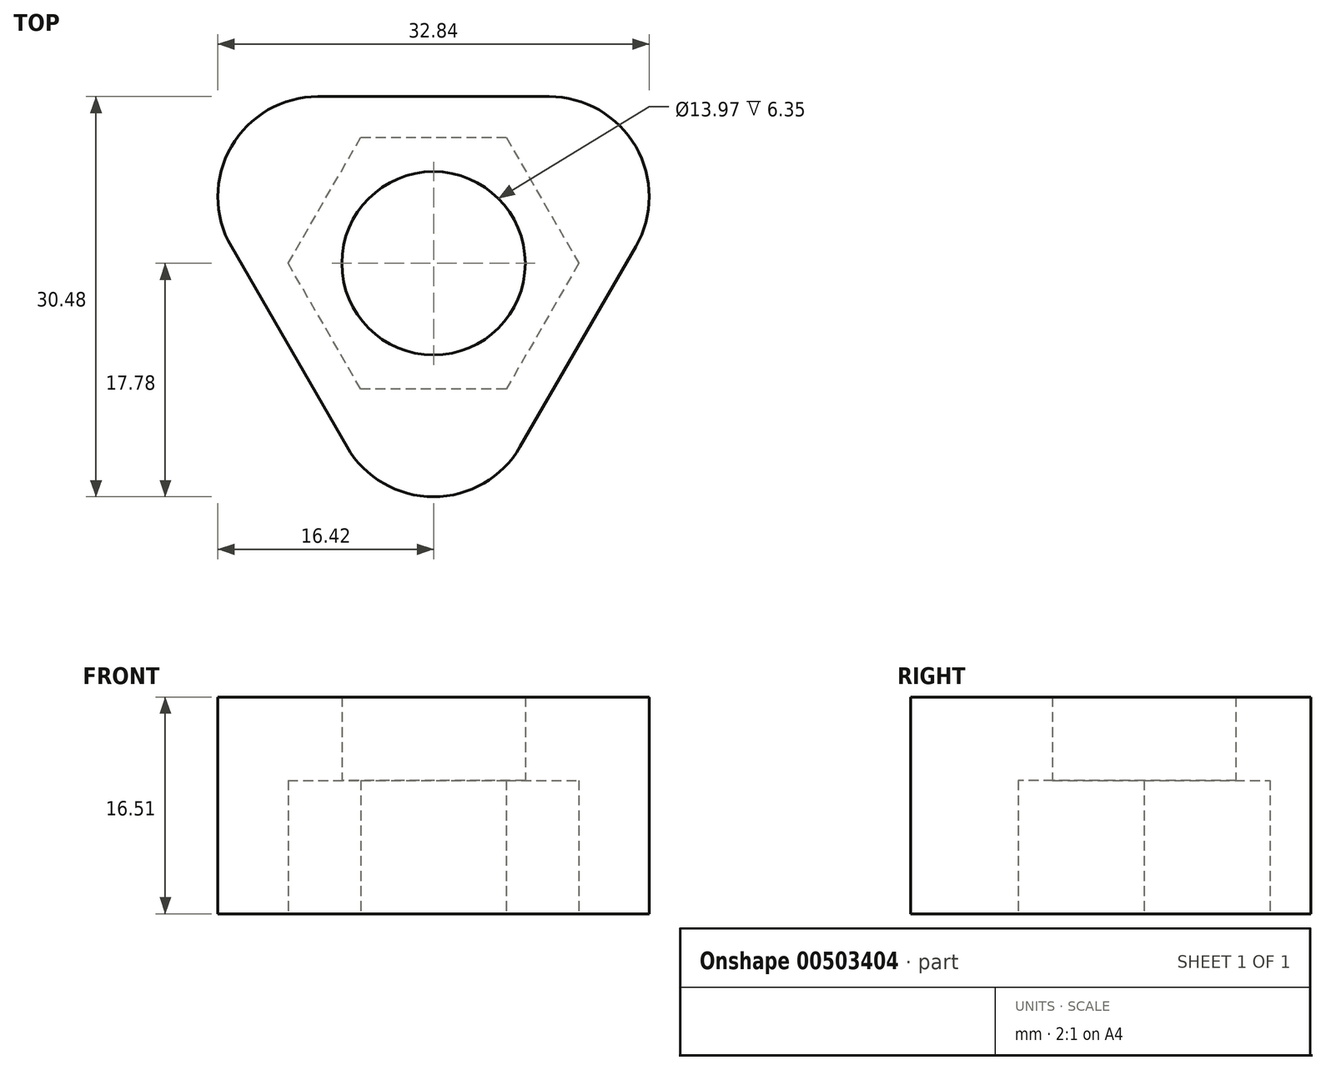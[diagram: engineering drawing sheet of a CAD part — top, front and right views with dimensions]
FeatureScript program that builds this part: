
annotation { "Feature Type Name" : "Feature", "Feature Type Description" : "" }
export const myFeature = defineFeature(function(context is Context, id is Id, definition is map)
    precondition{}
    {
        {
            var Q0;
            Q0=qCreatedBy(makeId("Top.planeOp"),FACE);
            var sketch = newSketch(context, id + "F0", { "sketchPlane" : qUnion([Q0])});
            skCircle(sketch, "E0.cCircle", {"center": v(0, 0) * mm, "radius": 9.59 * mm, "construction": true});
            skLineSegment(sketch, "E0.0", {"start": v(-5.54, 9.59) * mm, "end": v(5.54, 9.59) * mm});
            skLineSegment(sketch, "E0.1", {"start": v(5.54, 9.59) * mm, "end": v(11.07, 0) * mm});
            skLineSegment(sketch, "E0.2", {"start": v(11.07, 0) * mm, "end": v(5.54, -9.59) * mm});
            skLineSegment(sketch, "E0.3", {"start": v(5.54, -9.59) * mm, "end": v(-5.54, -9.59) * mm});
            skLineSegment(sketch, "E0.4", {"start": v(-5.54, -9.59) * mm, "end": v(-11.07, 0) * mm});
            skLineSegment(sketch, "E0.5", {"start": v(-11.07, 0) * mm, "end": v(-5.54, 9.59) * mm});
            skPoint(sketch, "E0.0.midPoint", {"position": v(0, 9.59) * mm});
            skCircle(sketch, "E1.cCircle", {"center": v(0, 0) * mm, "radius": 12.7 * mm, "construction": true});
            skLineSegment(sketch, "E1.0", {"start": v(-22, 12.7) * mm, "end": v(22, 12.7) * mm});
            skLineSegment(sketch, "E1.1", {"start": v(22, 12.7) * mm, "end": v(0, -25.4) * mm});
            skLineSegment(sketch, "E1.2", {"start": v(0, -25.4) * mm, "end": v(-22, 12.7) * mm});
            skPoint(sketch, "E1.0.midPoint", {"position": v(0, 12.7) * mm});
            skSolve(sketch);
        }
        {
            var Q0;
            Q0=makeQuery(id+"F0.imprint","IMPRINT",FACE,{"disambiguationData":[TD([[makeQuery(id+"F0.imprint","IMPRINT",EDGE,{"derivedFrom":sQuery(id+"F0.wireOp",EDGE,"E0.0")}),1.0]])]});
            extrude(context, id + "F1", {"entities" : qUnion([Q0]), "depth" : 10.16 * mm});
        }
        {
            var Q0;
            Q0=makeQuery(id+"F1.opExtrude","CAP_FACE",FACE,{"disambiguationData":[OSD([sQuery(id+"F0.wireOp",EDGE,"E0.0"),sQuery(id+"F0.wireOp",EDGE,"E0.1"),sQuery(id+"F0.wireOp",EDGE,"E0.2"),sQuery(id+"F0.wireOp",EDGE,"E0.3"),sQuery(id+"F0.wireOp",EDGE,"E0.4"),sQuery(id+"F0.wireOp",EDGE,"E0.5"),sQuery(id+"F0.wireOp",EDGE,"E1.0"),sQuery(id+"F0.wireOp",EDGE,"E1.1"),sQuery(id+"F0.wireOp",EDGE,"E1.2")])],"isStart":false});
            var sketch = newSketch(context, id + "F2", { "sketchPlane" : qUnion([Q0])});
            skCircle(sketch, "E2", {"center": v(0, 0) * mm, "radius": 6.99 * mm});
            skCircle(sketch, "E3.cCircle", {"center": v(0, 0) * mm, "radius": 12.7 * mm, "construction": true});
            skLineSegment(sketch, "E3.0", {"start": v(-22, 12.7) * mm, "end": v(22, 12.7) * mm});
            skLineSegment(sketch, "E3.1", {"start": v(22, 12.7) * mm, "end": v(0, -25.4) * mm});
            skLineSegment(sketch, "E3.2", {"start": v(0, -25.4) * mm, "end": v(-22, 12.7) * mm});
            skPoint(sketch, "E3.0.midPoint", {"position": v(0, 12.7) * mm});
            skSolve(sketch);
        }
        {
            var Q0;
            Q0=makeQuery(id+"F2.imprint","IMPRINT",FACE,{"disambiguationData":[TD([[makeQuery(id+"F2.imprint","IMPRINT",EDGE,{"derivedFrom":sQuery(id+"F2.wireOp",EDGE,"E3.0")}),-1.0]])]});
            var Q1;
            Q1=makeQuery(id+"F2.imprint","IMPRINT",FACE,{"disambiguationData":[TD([[makeQuery(id+"F2.imprint","IMPRINT",EDGE,{"derivedFrom":sQuery(id+"F2.wireOp",EDGE,"E2")}),-1.0]])]});
            extrude(context, id + "F3", {"entities" : qUnion([Q0, Q1]), "operationType" : NewBodyOperationType.ADD, "depth" : 6.35 * mm});
        }
        {
            var Q0;
            Q0=makeQuery(id+"F3.boolean.opBoolean","MERGE",EDGE,{"derivedFrom":[makeQuery(id+"F1.opExtrude","SWEPT_EDGE",EDGE,{"disambiguationData":[OSD([sQuery(id+"F0.wireOp",EDGE,"E1.0"),sQuery(id+"F0.wireOp",EDGE,"E1.2")])]}),makeQuery(id+"F3.opExtrude","SWEPT_EDGE",EDGE,{"disambiguationData":[OSD([sQuery(id+"F2.wireOp",EDGE,"E3.0"),sQuery(id+"F2.wireOp",EDGE,"E3.2")])]})]});
            var Q1;
            Q1=makeQuery(id+"F3.boolean.opBoolean","MERGE",EDGE,{"derivedFrom":[makeQuery(id+"F1.opExtrude","SWEPT_EDGE",EDGE,{"disambiguationData":[OSD([sQuery(id+"F0.wireOp",EDGE,"E1.0"),sQuery(id+"F0.wireOp",EDGE,"E1.1")])]}),makeQuery(id+"F3.opExtrude","SWEPT_EDGE",EDGE,{"disambiguationData":[OSD([sQuery(id+"F2.wireOp",EDGE,"E3.0"),sQuery(id+"F2.wireOp",EDGE,"E3.1")])]})]});
            var Q2;
            Q2=makeQuery(id+"F3.boolean.opBoolean","MERGE",EDGE,{"derivedFrom":[makeQuery(id+"F1.opExtrude","SWEPT_EDGE",EDGE,{"disambiguationData":[OSD([sQuery(id+"F0.wireOp",EDGE,"E1.1"),sQuery(id+"F0.wireOp",EDGE,"E1.2")])]}),makeQuery(id+"F3.opExtrude","SWEPT_EDGE",EDGE,{"disambiguationData":[OSD([sQuery(id+"F2.wireOp",EDGE,"E3.1"),sQuery(id+"F2.wireOp",EDGE,"E3.2")])]})]});
            fillet(context, id + "F4", {"entities" : qUnion([Q0, Q1, Q2]), "radius" : 7.62 * mm, "tangentPropagation" : true, "allowEdgeOverflow" : false});
        }
    });
